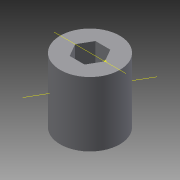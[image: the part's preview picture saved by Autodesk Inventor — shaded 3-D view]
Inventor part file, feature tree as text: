
AUTODESK INVENTOR PART (.ipt)
format: ipt  version: 2015 SP1 (Build 190203100, 203)  size: 108,544 bytes
history: native  units: mm
features: other x4, extrude x2, sketch x2
ambient origin geometry x8: Origin, YZ Plane, XZ Plane, XY Plane, X Axis, Y Axis, Z Axis, Center Point
bodies: Body1 (feature_tree)
feature tree (8):
  other  "Sólido1"
  extrude  "Extrusión1"  Depth=12.0mm
  extrude  "Extrusión2"  Depth=6.0mm TaperAngle=0.0deg
  other  "Eje de trabajo1"
  other  "Eje de trabajo2"
  sketch  "Boceto1"  dims[d0=8.0mm d1=12.0mm]
  sketch  "Boceto2"  dims[d2=7.0mm d3=0.0mm d4=6.0mm d5=0.0mm]
  other  "Punto de trabajo1"
